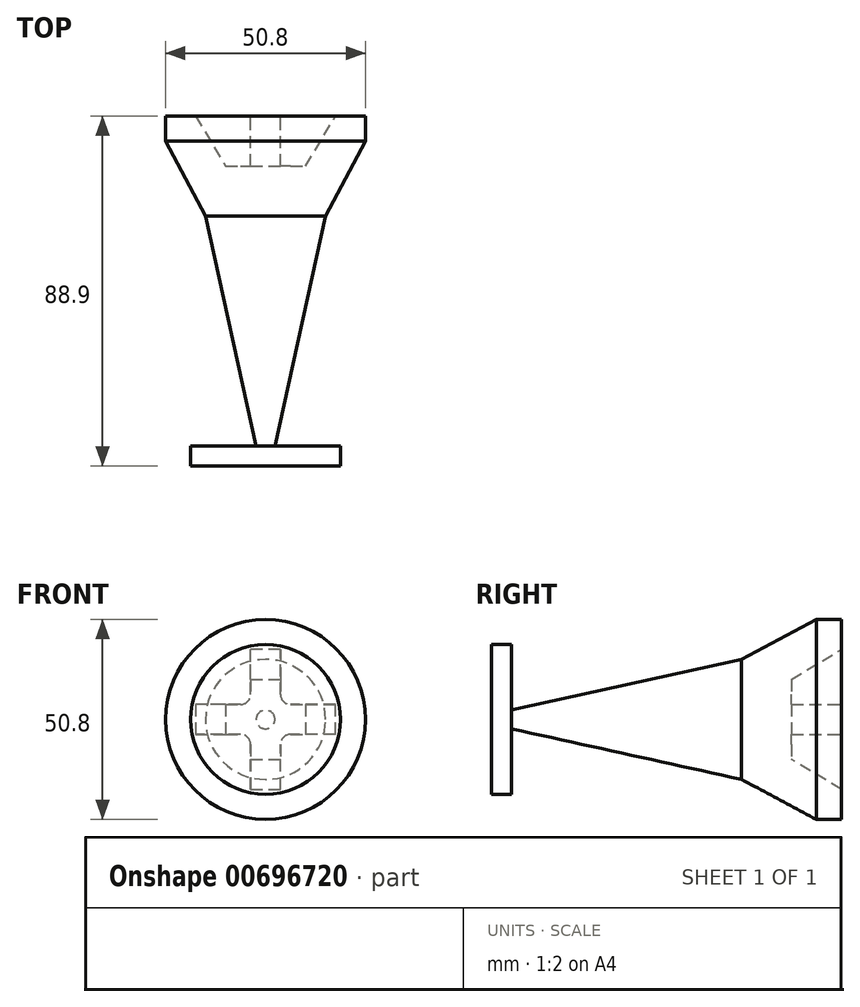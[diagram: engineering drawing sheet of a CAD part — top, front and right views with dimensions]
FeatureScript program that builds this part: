
annotation { "Feature Type Name" : "Feature", "Feature Type Description" : "" }
export const myFeature = defineFeature(function(context is Context, id is Id, definition is map)
    precondition{}
    {
        {
            var Q0;
            Q0=qCreatedBy(makeId("Top.planeOp"),FACE);
            var sketch = newSketch(context, id + "F0", { "sketchPlane" : qUnion([Q0])});
            skLineSegment(sketch, "E0.bottom", {"start": v(-12.7, -12.7) * mm, "end": v(12.7, -12.7) * mm});
            skLineSegment(sketch, "E0.top", {"start": v(-12.7, 12.7) * mm, "end": v(12.7, 12.7) * mm});
            skLineSegment(sketch, "E0.left", {"start": v(-12.7, -12.7) * mm, "end": v(-12.7, 12.7) * mm});
            skLineSegment(sketch, "E0.right", {"start": v(12.7, -12.7) * mm, "end": v(12.7, 12.7) * mm});
            skPoint(sketch, "E0.middle", {"position": v(0, 0) * mm});
            skSolve(sketch);
        }
        {
            var Q0;
            Q0=makeQuery(id+"F0.imprint","IMPRINT",FACE,{"disambiguationData":[TD([[makeQuery(id+"F0.imprint","IMPRINT",EDGE,{"derivedFrom":sQuery(id+"F0.wireOp",EDGE,"E0.bottom")}),1.0]])]});
            var Q1;
            Q1=sQuery(id+"F0.wireOp",EDGE,"E0.left");
            revolve(context, id + "F1", {"entities" : qUnion([Q0]), "axis" : qUnion([Q1]), "revolveType" : RevolveType.FULL});
        }
        {
            var Q0;
            Q0=makeQuery(id+"F1.opRevolve","SWEPT_EDGE",EDGE,{"disambiguationData":[OSD([sQuery(id+"F0.wireOp",EDGE,"E0.bottom"),sQuery(id+"F0.wireOp",EDGE,"E0.right")])]});
            chamfer(context, id + "F2", {"entities" : qUnion([Q0]), "chamferType" : ChamferType.TWO_OFFSETS, "width1" : 10.16 * mm, "oppositeDirection" : false, "width2" : 19.05 * mm, "tangentPropagation" : true});
        }
        {
            var Q0;
            Q0=makeQuery(id+"F1.opRevolve","SWEPT_FACE",FACE,{"disambiguationData":[OSD([sQuery(id+"F0.wireOp",EDGE,"E0.top")])]});
            var sketch = newSketch(context, id + "F3", { "sketchPlane" : qUnion([Q0])});
            skLineSegment(sketch, "E1.bottom", {"start": v(16.51, 10.16) * mm, "end": v(8.9, 10.16) * mm});
            skLineSegment(sketch, "E1.top", {"start": v(16.51, -10.16) * mm, "end": v(8.9, -10.16) * mm});
            skLineSegment(sketch, "E1.left", {"start": v(22.86, 3.81) * mm, "end": v(22.86, -3.81) * mm});
            skLineSegment(sketch, "E1.right", {"start": v(2.54, 3.81) * mm, "end": v(2.54, -3.81) * mm});
            skPoint(sketch, "E1.middle", {"position": v(12.7, 0) * mm});
            skLineSegment(sketch, "E2.left", {"start": v(16.51, 10.16) * mm, "end": v(16.51, -10.16) * mm});
            skLineSegment(sketch, "E2.right", {"start": v(8.9, 10.16) * mm, "end": v(8.9, -10.16) * mm});
            skLineSegment(sketch, "E3.bottom", {"start": v(22.86, 3.81) * mm, "end": v(2.54, 3.81) * mm});
            skLineSegment(sketch, "E3.top", {"start": v(22.86, -3.81) * mm, "end": v(2.54, -3.81) * mm});
            skPoint(sketch, "E4.orphan", {"position": v(2.54, 10.16) * mm});
            skPoint(sketch, "E5.orphan", {"position": v(22.86, 10.16) * mm});
            skPoint(sketch, "E6.orphan", {"position": v(2.54, -10.16) * mm});
            skPoint(sketch, "E7.orphan", {"position": v(22.86, -10.16) * mm});
            skSolve(sketch);
        }
        {
            var Q0;
            {var subQ0=sQuery(id+"F3.wireOp",EDGE,"E1.bottom");Q0=makeQuery(id+"F3.imprint","IMPRINT",FACE,{"disambiguationData":[TD([[makeQuery(id+"F3.imprint","IMPRINT",EDGE,{"derivedFrom":subQ0}),1.0]])]});}
            var Q1;
            {var subQ5=sQuery(id+"F3.wireOp",EDGE,"E1.right");Q1=makeQuery(id+"F3.imprint","IMPRINT",FACE,{"disambiguationData":[TD([[makeQuery(id+"F3.imprint","IMPRINT",EDGE,{"derivedFrom":subQ5}),1.0]])]});}
            var Q2;
            {var subQ0=sQuery(id+"F3.wireOp",EDGE,"E3.bottom");var subQ1=sQuery(id+"F3.wireOp",EDGE,"E2.left");var subQ2=makeQuery(id+"F3.imprint","INTERSECT",VERTEX,{"derivedFrom":[subQ1,subQ0]});Q2=makeQuery(id+"F3.imprint","IMPRINT",FACE,{"disambiguationData":[TD([[makeQuery(id+"F3.imprint","IMPRINT",EDGE,{"disambiguationData":[TD([[subQ2,-1.0]])],"derivedFrom":subQ1}),-1.0]])]});}
            var Q3;
            {var subQ5=sQuery(id+"F3.wireOp",EDGE,"E1.left");Q3=makeQuery(id+"F3.imprint","IMPRINT",FACE,{"disambiguationData":[TD([[makeQuery(id+"F3.imprint","IMPRINT",EDGE,{"derivedFrom":subQ5}),-1.0]])]});}
            var Q4;
            {var subQ0=sQuery(id+"F3.wireOp",EDGE,"E1.top");Q4=makeQuery(id+"F3.imprint","IMPRINT",FACE,{"disambiguationData":[TD([[makeQuery(id+"F3.imprint","IMPRINT",EDGE,{"derivedFrom":subQ0}),-1.0]])]});}
            extrude(context, id + "F4", {"entities" : qUnion([Q0, Q1, Q2, Q3, Q4]), "operationType" : NewBodyOperationType.REMOVE, "endBound" : BoundingType.SYMMETRIC, "oppositeDirection" : true, "depth" : 25.4 * mm, "offsetDistance" : 25.4 * mm});
        }
        {
            var Q0;
            Q0=makeQuery(id+"F4.boolean.opBoolean","INTERSECT",EDGE,{"derivedFrom":[makeQuery(id+"F1.opRevolve","SWEPT_FACE",FACE,{"disambiguationData":[OSD([sQuery(id+"F0.wireOp",EDGE,"E0.top")])]}),makeQuery(id+"F4.opExtrude","SWEPT_FACE",FACE,{"disambiguationData":[OSD([sQuery(id+"F3.wireOp",EDGE,"E1.bottom")])]})]});
            var Q1;
            Q1=makeQuery(id+"F4.boolean.opBoolean","INTERSECT",EDGE,{"derivedFrom":[makeQuery(id+"F1.opRevolve","SWEPT_FACE",FACE,{"disambiguationData":[OSD([sQuery(id+"F0.wireOp",EDGE,"E0.top")])]}),makeQuery(id+"F4.opExtrude","SWEPT_FACE",FACE,{"disambiguationData":[OSD([sQuery(id+"F3.wireOp",EDGE,"E1.right")])]})]});
            var Q2;
            Q2=makeQuery(id+"F4.boolean.opBoolean","INTERSECT",EDGE,{"derivedFrom":[makeQuery(id+"F1.opRevolve","SWEPT_FACE",FACE,{"disambiguationData":[OSD([sQuery(id+"F0.wireOp",EDGE,"E0.top")])]}),makeQuery(id+"F4.opExtrude","SWEPT_FACE",FACE,{"disambiguationData":[OSD([sQuery(id+"F3.wireOp",EDGE,"E1.left")])]})]});
            var Q3;
            Q3=makeQuery(id+"F4.boolean.opBoolean","INTERSECT",EDGE,{"derivedFrom":[makeQuery(id+"F1.opRevolve","SWEPT_FACE",FACE,{"disambiguationData":[OSD([sQuery(id+"F0.wireOp",EDGE,"E0.top")])]}),makeQuery(id+"F4.opExtrude","SWEPT_FACE",FACE,{"disambiguationData":[OSD([sQuery(id+"F3.wireOp",EDGE,"E1.top")])]})]});
            chamfer(context, id + "F5", {"entities" : qUnion([Q0, Q1, Q2, Q3]), "chamferType" : ChamferType.TWO_OFFSETS, "width1" : 7.62 * mm, "oppositeDirection" : false, "width2" : 12.7 * mm, "tangentPropagation" : true});
        }
        {
            var Q0;
            Q0=makeQuery(id+"F4.boolean.opBoolean","COPY",EDGE,{"derivedFrom":makeQuery(id+"F4.opExtrude","SWEPT_EDGE",EDGE,{"disambiguationData":[OSD([sQuery(id+"F3.wireOp",EDGE,"E2.right"),sQuery(id+"F3.wireOp",EDGE,"E3.top")])]})});
            var Q1;
            Q1=makeQuery(id+"F4.boolean.opBoolean","COPY",EDGE,{"derivedFrom":makeQuery(id+"F4.opExtrude","SWEPT_EDGE",EDGE,{"disambiguationData":[OSD([sQuery(id+"F3.wireOp",EDGE,"E2.left"),sQuery(id+"F3.wireOp",EDGE,"E3.top")])]})});
            var Q2;
            Q2=makeQuery(id+"F4.boolean.opBoolean","COPY",EDGE,{"derivedFrom":makeQuery(id+"F4.opExtrude","SWEPT_EDGE",EDGE,{"disambiguationData":[OSD([sQuery(id+"F3.wireOp",EDGE,"E2.right"),sQuery(id+"F3.wireOp",EDGE,"E3.bottom")])]})});
            var Q3;
            Q3=makeQuery(id+"F4.boolean.opBoolean","COPY",EDGE,{"derivedFrom":makeQuery(id+"F4.opExtrude","SWEPT_EDGE",EDGE,{"disambiguationData":[OSD([sQuery(id+"F3.wireOp",EDGE,"E2.left"),sQuery(id+"F3.wireOp",EDGE,"E3.bottom")])]})});
            fillet(context, id + "F6", {"entities" : qUnion([Q0, Q1, Q2, Q3]), "radius" : 2.54 * mm, "tangentPropagation" : true, "allowEdgeOverflow" : false});
        }
        {
            var Q0;
            Q0=makeQuery(id+"F1.opRevolve","SWEPT_FACE",FACE,{"disambiguationData":[OSD([sQuery(id+"F0.wireOp",EDGE,"E0.bottom")])]});
            var sketch = newSketch(context, id + "F7", { "sketchPlane" : qUnion([Q0])});
            skCircle(sketch, "E8", {"center": v(-12.7, 0) * mm, "radius": 15.24 * mm});
            skSolve(sketch);
        }
        {
            var Q0;
            Q0=makeQuery(id+"F7.imprint","IMPRINT",FACE,{"disambiguationData":[TD([[makeQuery(id+"F7.imprint","IMPRINT",EDGE,{"derivedFrom":sQuery(id+"F7.wireOp",EDGE,"E8")}),1.0]])]});
            extrude(context, id + "F8", {"entities" : qUnion([Q0]), "operationType" : NewBodyOperationType.ADD, "depth" : 63.5 * mm, "offsetDistance" : 25.4 * mm});
        }
        {
            var Q0;
            Q0=makeQuery(id+"F8.opExtrude","CAP_EDGE",EDGE,{"disambiguationData":[OSD([sQuery(id+"F7.wireOp",EDGE,"E8")])],"isStart":false});
            chamfer(context, id + "F9", {"entities" : qUnion([Q0]), "chamferType" : ChamferType.TWO_OFFSETS, "width1" : 13.97 * mm, "oppositeDirection" : false, "width2" : 63.5 * mm, "tangentPropagation" : true});
        }
        {
            var Q0;
            Q0=makeQuery(id+"F8.opExtrude","CAP_FACE",FACE,{"disambiguationData":[OSD([sQuery(id+"F7.wireOp",EDGE,"E8")])],"isStart":false});
            var sketch = newSketch(context, id + "F10", { "sketchPlane" : qUnion([Q0])});
            skCircle(sketch, "E9", {"center": v(-12.7, 0) * mm, "radius": 19.05 * mm});
            skSolve(sketch);
        }
        {
            var Q0;
            Q0=makeQuery(id+"F10.imprint","IMPRINT",FACE,{"disambiguationData":[TD([[makeQuery(id+"F10.imprint","IMPRINT",EDGE,{"derivedFrom":sQuery(id+"F10.wireOp",EDGE,"E9")}),1.0]])]});
            extrude(context, id + "F11", {"entities" : qUnion([Q0]), "operationType" : NewBodyOperationType.ADD, "oppositeDirection" : true, "depth" : 5.08 * mm, "offsetDistance" : 25.4 * mm});
        }
    });
